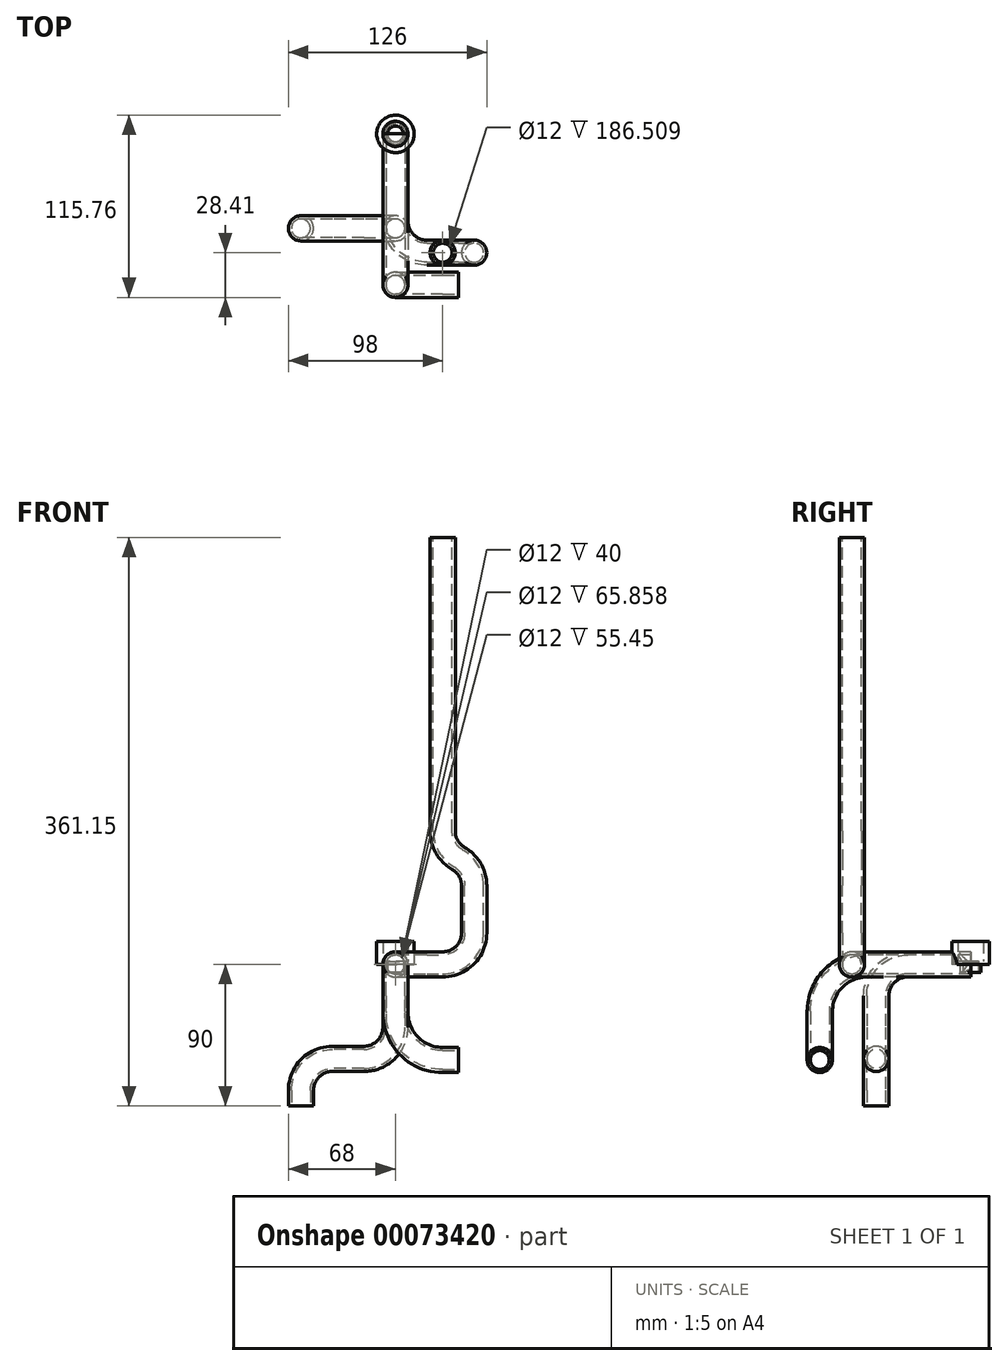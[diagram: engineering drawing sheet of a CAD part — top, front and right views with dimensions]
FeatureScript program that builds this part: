
annotation { "Feature Type Name" : "Feature", "Feature Type Description" : "" }
export const myFeature = defineFeature(function(context is Context, id is Id, definition is map)
    precondition{}
    {
        {
            var Q0;
            Q0=qCreatedBy(makeId("Front.planeOp"),FACE);
            var sketch = newSketch(context, id + "F0", { "sketchPlane" : qUnion([Q0])});
            skCircle(sketch, "E0", {"center": v(0, 0) * mm, "radius": 8 * mm});
            skCircle(sketch, "E1", {"center": v(0, 0) * mm, "radius": 6 * mm});
            skSolve(sketch);
        }
        {
            var Q0;
            Q0=qCreatedBy(makeId("Right.planeOp"),FACE);
            var sketch = newSketch(context, id + "F1", { "sketchPlane" : qUnion([Q0])});
            skLineSegment(sketch, "E2", {"start": v(0, 0) * mm, "end": v(-65.86, 0) * mm});
            skLineSegment(sketch, "E3", {"start": v(-95.86, -30) * mm, "end": v(-95.86, -30) * mm});
            skPoint(sketch, "E4.visualSharp", {"position": v(-95.86, 0) * mm});
            skArc(sketch, "E4.filletArc", {"start": v(-65.86, 0) * mm, "mid": v(-87.07, -8.79) * mm, "end": v(-95.86, -30) * mm});
            skSolve(sketch);
        }
        {
            var Q0;
            Q0 = qSketchRegion(id + "F0", true);
            var Q1;
            Q1 = qConstructionFilter(qBodyType(qCreatedBy(id + "F1" ,EDGE), BodyType.WIRE), ConstructionObject.NO);
            sweep(context, id + "F2", {"profiles" : qUnion([Q0]), "path" : qUnion([Q1])});
        }
        {
            var Q0;
            Q0=qCreatedBy(makeId("Top.planeOp"),FACE);
            var sketch = newSketch(context, id + "F3", { "sketchPlane" : qUnion([Q0])});
            skCircle(sketch, "E5", {"center": v(0, 0) * mm, "radius": 11.9 * mm});
            skCircle(sketch, "E6", {"center": v(0, 0) * mm, "radius": 8 * mm});
            skSolve(sketch);
        }
        {
            var Q0;
            Q0 = qSketchRegion(id + "F3", true);
            extrude(context, id + "F4", {"entities" : qUnion([Q0]), "depth" : 14.5 * mm});
        }
        {
            var Q0;
            Q0=makeQuery(id+"F4.opExtrude","CAP_FACE",FACE,{"disambiguationData":[OSD([sQuery(id+"F3.wireOp",EDGE,"E5"),sQuery(id+"F3.wireOp",EDGE,"E6")])],"isStart":true});
            var sketch = newSketch(context, id + "F5", { "sketchPlane" : qUnion([Q0])});
            skCircle(sketch, "E7", {"center": v(0, 0) * mm, "radius": 5 * mm});
            skCircle(sketch, "E8", {"center": v(0, 0) * mm, "radius": 8 * mm});
            skSolve(sketch);
        }
        {
            var Q0;
            Q0 = qSketchRegion(id + "F5", true);
            extrude(context, id + "F6", {"entities" : qUnion([Q0]), "operationType" : NewBodyOperationType.ADD, "oppositeDirection" : true, "depth" : 2 * mm});
        }
        {
            var Q0;
            Q0=makeQuery(id+"F6.boolean.opBoolean","MERGE",FACE,{"derivedFrom":[makeQuery(id+"F4.opExtrude","CAP_FACE",FACE,{"disambiguationData":[OSD([sQuery(id+"F3.wireOp",EDGE,"E5"),sQuery(id+"F3.wireOp",EDGE,"E6")])],"isStart":true}),makeQuery(id+"F6.opExtrude","CAP_FACE",FACE,{"disambiguationData":[OSD([sQuery(id+"F5.wireOp",EDGE,"E7"),sQuery(id+"F5.wireOp",EDGE,"E8")])],"isStart":true})]});
            var sketch = newSketch(context, id + "F7", { "sketchPlane" : qUnion([Q0])});
            skCircle(sketch, "E9", {"center": v(0, 0) * mm, "radius": 5 * mm});
            skCircle(sketch, "E10", {"center": v(0, 0) * mm, "radius": 6.5 * mm});
            skSolve(sketch);
        }
        {
            var Q0;
            Q0 = qSketchRegion(id + "F7", true);
            extrude(context, id + "F8", {"entities" : qUnion([Q0]), "operationType" : NewBodyOperationType.ADD, "depth" : 5 * mm});
        }
        {
            var Q0;
            Q0=qCreatedBy(makeId("Front.planeOp"),FACE);
            cPlane(context, id + "F9", {"entities" : qUnion([Q0]), "cplaneType" : CPlaneType.OFFSET, "offset" : (100 - 1.72 - 2.42) * mm, "width" : 150 * mm, "height" : 150 * mm});
        }
        {
            var Q0;
            Q0=qCreatedBy(id+"F9.planeOp",FACE);
            var sketch = newSketch(context, id + "F10", { "sketchPlane" : qUnion([Q0])});
            skLineSegment(sketch, "E11", {"start": v(0, -30) * mm, "end": v(0, -30.76) * mm});
            skLineSegment(sketch, "E12", {"start": v(30, -60.76) * mm, "end": v(40, -60.76) * mm});
            skPoint(sketch, "E13.visualSharp", {"position": v(0, -60.76) * mm});
            skArc(sketch, "E13.filletArc", {"start": v(0, -30.76) * mm, "mid": v(8.79, -51.98) * mm, "end": v(30, -60.76) * mm});
            skSolve(sketch);
        }
        {
            var Q0;
            Q0=makeQuery(id+"F2.opSweep","CAP_FACE",FACE,{"disambiguationData":[OSD([sQuery(id+"F0.wireOp",EDGE,"E0"),sQuery(id+"F0.wireOp",EDGE,"E1"),sQuery(id+"F1.wireOp",VERTEX,"E3.end")])],"isStart":false});
            var Q1;
            Q1 = qConstructionFilter(qBodyType(qCreatedBy(id + "F10" ,EDGE), BodyType.WIRE), ConstructionObject.NO);
            sweep(context, id + "F11", {"operationType" : NewBodyOperationType.ADD, "profiles" : qUnion([Q0]), "path" : qUnion([Q1])});
        }
        {
            var Q0;
            Q0=qCreatedBy(makeId("Front.planeOp"),FACE);
            var sketch = newSketch(context, id + "F12", { "sketchPlane" : qUnion([Q0])});
            skCircle(sketch, "E14", {"center": v(0, 0) * mm, "radius": 6 * mm});
            skCircle(sketch, "E15", {"center": v(0, 0) * mm, "radius": 8 * mm});
            skSolve(sketch);
        }
        {
            var Q0;
            Q0=qCreatedBy(makeId("Top.planeOp"),FACE);
            var sketch = newSketch(context, id + "F13", { "sketchPlane" : qUnion([Q0])});
            skLineSegment(sketch, "E16", {"start": v(0, 0) * mm, "end": v(0, -55.45) * mm});
            skLineSegment(sketch, "E17", {"start": v(20, -75.45) * mm, "end": v(25, -75.45) * mm});
            skPoint(sketch, "E18.visualSharp", {"position": v(0, -75.45) * mm});
            skArc(sketch, "E18.filletArc", {"start": v(0, -55.45) * mm, "mid": v(5.86, -69.6) * mm, "end": v(20, -75.45) * mm});
            skSolve(sketch);
        }
        {
            var Q0;
            Q0=qCreatedBy(makeId("Front.planeOp"),FACE);
            cPlane(context, id + "F14", {"entities" : qUnion([Q0]), "cplaneType" : CPlaneType.OFFSET, "offset" : 75.45 * mm, "width" : 150 * mm, "height" : 150 * mm});
        }
        {
            var Q0;
            Q0=qCreatedBy(id+"F14.planeOp",FACE);
            var sketch = newSketch(context, id + "F15", { "sketchPlane" : qUnion([Q0])});
            skLineSegment(sketch, "E19", {"start": v(25, 0) * mm, "end": v(30, 0) * mm});
            skLineSegment(sketch, "E20", {"start": v(50, 20) * mm, "end": v(50, 50) * mm});
            skPoint(sketch, "E21.visualSharp", {"position": v(50, 0) * mm});
            skArc(sketch, "E21.filletArc", {"start": v(30, 0) * mm, "mid": v(44.14, 5.86) * mm, "end": v(50, 20) * mm});
            skSolve(sketch);
        }
        {
            var Q0;
            Q0 = qSketchRegion(id + "F12", true);
            var Q1;
            Q1 = qConstructionFilter(qBodyType(qCreatedBy(id + "F13" ,EDGE), BodyType.WIRE), ConstructionObject.NO);
            sweep(context, id + "F16", {"profiles" : qUnion([Q0]), "path" : qUnion([Q1])});
        }
        {
            var Q0;
            Q0=makeQuery(id+"F16.opSweep","CAP_FACE",FACE,{"disambiguationData":[OSD([sQuery(id+"F12.wireOp",EDGE,"E14"),sQuery(id+"F12.wireOp",EDGE,"E15"),sQuery(id+"F13.wireOp",VERTEX,"E17.end")])],"isStart":false});
            var Q1;
            Q1 = qConstructionFilter(qBodyType(qCreatedBy(id + "F15" ,EDGE), BodyType.WIRE), ConstructionObject.NO);
            sweep(context, id + "F17", {"operationType" : NewBodyOperationType.ADD, "profiles" : qUnion([Q0]), "path" : qUnion([Q1])});
        }
        {
            var Q0;
            Q0=qCreatedBy(id+"F14.planeOp",FACE);
            var sketch = newSketch(context, id + "F18", { "sketchPlane" : qUnion([Q0])});
            skArc(sketch, "E22", {"start": v(50, 50) * mm, "mid": v(47.32, 60) * mm, "end": v(40, 67.32) * mm});
            skLineSegment(sketch, "E23", {"start": v(50, 50) * mm, "end": v(50, 16.4) * mm, "construction": true});
            skArc(sketch, "E24", {"start": v(30, 84.64) * mm, "mid": v(32.68, 74.64) * mm, "end": v(40, 67.32) * mm});
            skLineSegment(sketch, "E25", {"start": v(30, 84.64) * mm, "end": v(30, 271.15) * mm});
            skSolve(sketch);
        }
        {
            var Q0;
            Q0=makeQuery(id+"F17.opSweep","CAP_FACE",FACE,{"disambiguationData":[OSD([sQuery(id+"F12.wireOp",EDGE,"E14"),sQuery(id+"F12.wireOp",EDGE,"E15"),sQuery(id+"F13.wireOp",VERTEX,"E17.end"),sQuery(id+"F15.wireOp",VERTEX,"E20.end")])],"isStart":false});
            var Q1;
            Q1 = qConstructionFilter(qBodyType(qCreatedBy(id + "F18" ,EDGE), BodyType.WIRE), ConstructionObject.NO);
            sweep(context, id + "F19", {"operationType" : NewBodyOperationType.ADD, "profiles" : qUnion([Q0]), "path" : qUnion([Q1])});
        }
        {
            var Q0;
            Q0=qCreatedBy(makeId("Front.planeOp"),FACE);
            var sketch = newSketch(context, id + "F20", { "sketchPlane" : qUnion([Q0])});
            skCircle(sketch, "E26", {"center": v(0, 0) * mm, "radius": 6 * mm});
            skCircle(sketch, "E27", {"center": v(0, 0) * mm, "radius": 8 * mm});
            skSolve(sketch);
        }
        {
            var Q0;
            Q0=qCreatedBy(makeId("Right.planeOp"),FACE);
            var sketch = newSketch(context, id + "F21", { "sketchPlane" : qUnion([Q0])});
            skLineSegment(sketch, "E28", {"start": v(0, 0) * mm, "end": v(-40, 0) * mm});
            skLineSegment(sketch, "E29", {"start": v(-60, -20) * mm, "end": v(-60, -40) * mm});
            skPoint(sketch, "E30.visualSharp", {"position": v(-60, 0) * mm});
            skArc(sketch, "E30.filletArc", {"start": v(-40, 0) * mm, "mid": v(-54.14, -5.86) * mm, "end": v(-60, -20) * mm});
            skSolve(sketch);
        }
        {
            var Q0;
            Q0 = qSketchRegion(id + "F20", true);
            var Q1;
            Q1 = qConstructionFilter(qBodyType(qCreatedBy(id + "F21" ,EDGE), BodyType.WIRE), ConstructionObject.NO);
            sweep(context, id + "F22", {"profiles" : qUnion([Q0]), "path" : qUnion([Q1])});
        }
        {
            var Q0;
            Q0=qCreatedBy(makeId("Front.planeOp"),FACE);
            cPlane(context, id + "F23", {"entities" : qUnion([Q0]), "cplaneType" : CPlaneType.OFFSET, "offset" : 40 * mm, "width" : 150 * mm, "height" : 150 * mm});
        }
        {
            var Q0;
            Q0=qCreatedBy(id+"F23.planeOp",FACE);
            var sketch = newSketch(context, id + "F24", { "sketchPlane" : qUnion([Q0])});
            skLineSegment(sketch, "E31", {"start": v(0, -40) * mm, "end": v(0, -40) * mm});
            skLineSegment(sketch, "E32", {"start": v(-20, -60) * mm, "end": v(-40, -60) * mm});
            skPoint(sketch, "E33.visualSharp", {"position": v(0, -60) * mm});
            skArc(sketch, "E33.filletArc", {"start": v(-20, -60) * mm, "mid": v(-5.86, -54.14) * mm, "end": v(0, -40) * mm});
            skLineSegment(sketch, "E34", {"start": v(-60, -80) * mm, "end": v(-60, -90) * mm});
            skPoint(sketch, "E35.visualSharp", {"position": v(-60, -60) * mm});
            skArc(sketch, "E35.filletArc", {"start": v(-40, -60) * mm, "mid": v(-54.14, -65.86) * mm, "end": v(-60, -80) * mm});
            skSolve(sketch);
        }
        {
            var Q0;
            Q0=makeQuery(id+"F22.opSweep","CAP_FACE",FACE,{"disambiguationData":[OSD([sQuery(id+"F20.wireOp",EDGE,"E26"),sQuery(id+"F20.wireOp",EDGE,"E27"),sQuery(id+"F21.wireOp",VERTEX,"E29.end")])],"isStart":false});
            var Q1;
            Q1 = qConstructionFilter(qBodyType(qCreatedBy(id + "F24" ,EDGE), BodyType.WIRE), ConstructionObject.NO);
            sweep(context, id + "F25", {"operationType" : NewBodyOperationType.ADD, "profiles" : qUnion([Q0]), "path" : qUnion([Q1])});
        }
    });
